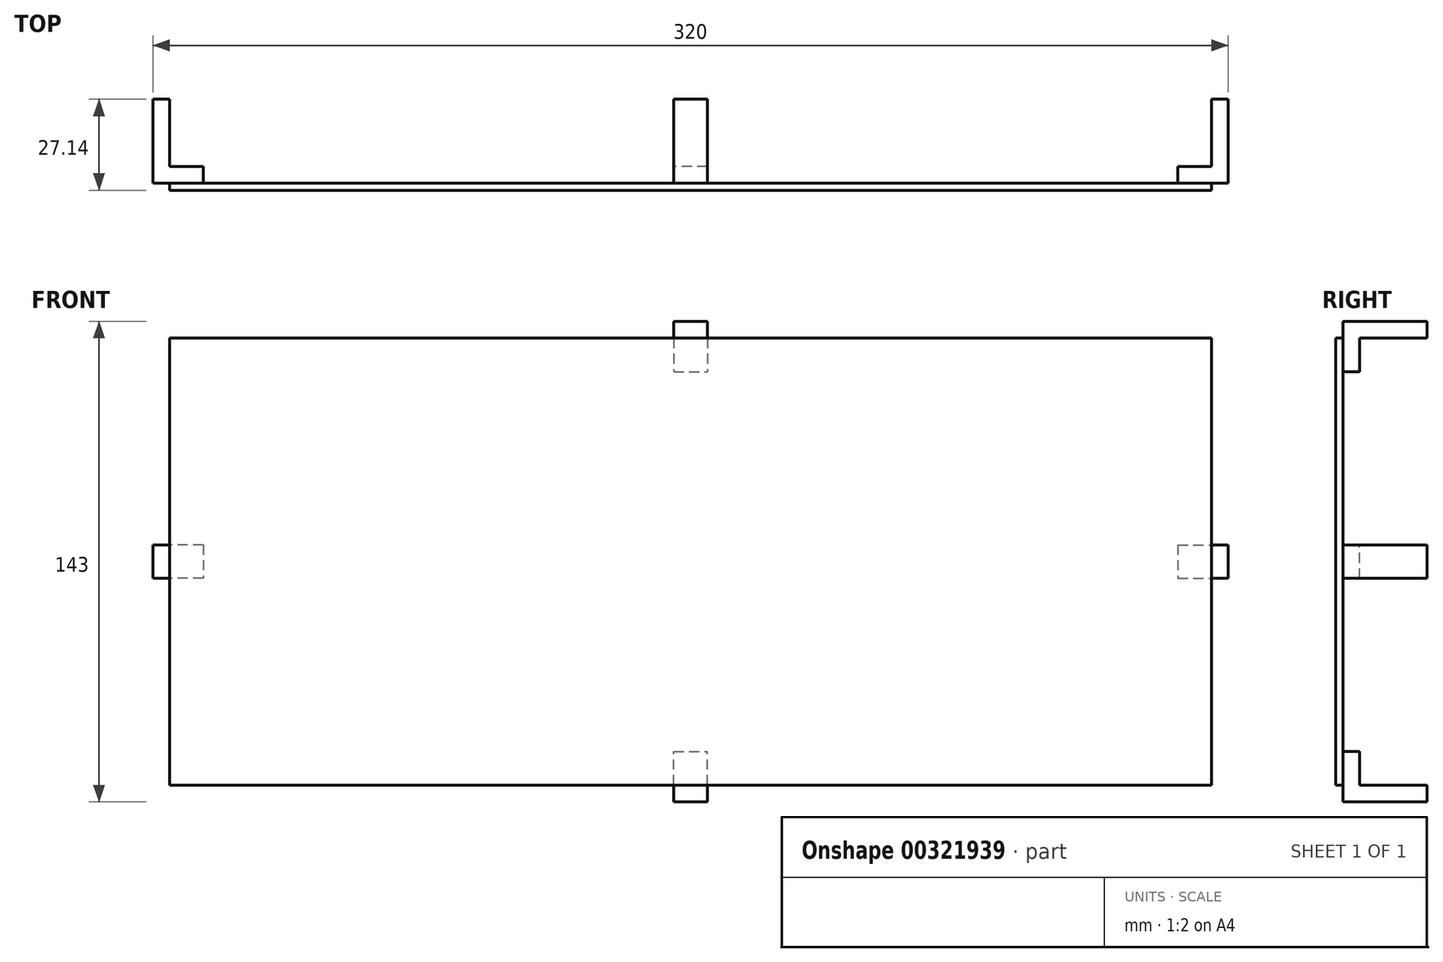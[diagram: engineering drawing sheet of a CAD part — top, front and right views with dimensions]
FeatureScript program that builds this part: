
annotation { "Feature Type Name" : "Feature", "Feature Type Description" : "" }
export const myFeature = defineFeature(function(context is Context, id is Id, definition is map)
    precondition{}
    {
        {
            var Q0;
            Q0=qCreatedBy(makeId("Front.planeOp"),FACE);
            var sketch = newSketch(context, id + "F0", { "sketchPlane" : qUnion([Q0])});
            skLineSegment(sketch, "E0.bottom", {"start": v(155, 66.5) * mm, "end": v(-155, 66.5) * mm});
            skLineSegment(sketch, "E0.top", {"start": v(155, -66.5) * mm, "end": v(-155, -66.5) * mm});
            skLineSegment(sketch, "E0.left", {"start": v(155, 66.5) * mm, "end": v(155, -66.5) * mm});
            skLineSegment(sketch, "E0.right", {"start": v(-155, 66.5) * mm, "end": v(-155, -66.5) * mm});
            skPoint(sketch, "E0.middle", {"position": v(0, 0) * mm});
            skSolve(sketch);
        }
        {
            var Q0;
            Q0 = qSketchRegion(id + "F0", true);
            extrude(context, id + "F1", {"entities" : qUnion([Q0]), "endBound" : BoundingType.SYMMETRIC, "depth" : 2.14 * mm});
        }
        {
            var Q0;
            Q0=makeQuery(id+"F1.opExtrude","CAP_FACE",FACE,{"disambiguationData":[OSD([sQuery(id+"F0.wireOp",EDGE,"E0.bottom"),sQuery(id+"F0.wireOp",EDGE,"E0.top"),sQuery(id+"F0.wireOp",EDGE,"E0.left"),sQuery(id+"F0.wireOp",EDGE,"E0.right")])],"isStart":true});
            var sketch = newSketch(context, id + "F2", { "sketchPlane" : qUnion([Q0])});
            skLineSegment(sketch, "E1.top", {"start": v(5, 56.5) * mm, "end": v(-5, 56.5) * mm});
            skLineSegment(sketch, "E1.left", {"start": v(5, 71.5) * mm, "end": v(5, 56.5) * mm});
            skLineSegment(sketch, "E1.right", {"start": v(-5, 71.5) * mm, "end": v(-5, 56.5) * mm});
            skPoint(sketch, "E1.middle", {"position": v(0, 66.5) * mm});
            skLineSegment(sketch, "E2", {"start": v(-5, 71.5) * mm, "end": v(5, 71.5) * mm});
            skPoint(sketch, "E1.bottom.end.orphan", {"position": v(-5, 76.5) * mm});
            skPoint(sketch, "E3.orphan", {"position": v(5, 76.5) * mm});
            skLineSegment(sketch, "E4.bottom", {"start": v(-145, 5) * mm, "end": v(-160, 5) * mm});
            skLineSegment(sketch, "E4.top", {"start": v(-145, -5) * mm, "end": v(-160, -5) * mm});
            skLineSegment(sketch, "E4.left", {"start": v(-145, 5) * mm, "end": v(-145, -5) * mm});
            skPoint(sketch, "E4.middle", {"position": v(-155, 0) * mm});
            skLineSegment(sketch, "E5", {"start": v(-160, 5) * mm, "end": v(-160, -5) * mm});
            skPoint(sketch, "E4.right.start.orphan", {"position": v(-165, 5) * mm});
            skPoint(sketch, "E6.orphan", {"position": v(-165, -5) * mm});
            skLineSegment(sketch, "E7.MirrorCS", {"start": v(5, -71.5) * mm, "end": v(5, -56.5) * mm});
            skLineSegment(sketch, "E8.MirrorCS", {"start": v(-5, -71.5) * mm, "end": v(-5, -56.5) * mm});
            skLineSegment(sketch, "E9.MirrorCS", {"start": v(-5, -71.5) * mm, "end": v(5, -71.5) * mm});
            skPoint(sketch, "E10.MirrorP", {"position": v(0, -66.5) * mm});
            skLineSegment(sketch, "E11.MirrorCS", {"start": v(5, -56.5) * mm, "end": v(-5, -56.5) * mm});
            skLineSegment(sketch, "E12.MirrorCS", {"start": v(145, 5) * mm, "end": v(145, -5) * mm});
            skPoint(sketch, "E13.MirrorP", {"position": v(165, -5) * mm});
            skPoint(sketch, "E14.MirrorP", {"position": v(165, 5) * mm});
            skLineSegment(sketch, "E15.MirrorCS", {"start": v(160, 5) * mm, "end": v(160, -5) * mm});
            skPoint(sketch, "E16.MirrorP", {"position": v(155, 0) * mm});
            skLineSegment(sketch, "E17.MirrorCS", {"start": v(145, -5) * mm, "end": v(160, -5) * mm});
            skLineSegment(sketch, "E18.MirrorCS", {"start": v(145, 5) * mm, "end": v(160, 5) * mm});
            skSolve(sketch);
        }
        {
            var Q0;
            Q0 = qSketchRegion(id + "F2", true);
            extrude(context, id + "F3", {"entities" : qUnion([Q0]), "operationType" : NewBodyOperationType.ADD, "depth" : 5 * mm});
        }
        {
            var Q0;
            Q0=makeQuery(id+"F3.opExtrude","CAP_FACE",FACE,{"disambiguationData":[OSD([sQuery(id+"F2.wireOp",EDGE,"E1.bottom"),sQuery(id+"F2.wireOp",EDGE,"E1.top"),sQuery(id+"F2.wireOp",EDGE,"E1.left"),sQuery(id+"F2.wireOp",EDGE,"E1.right")])],"isStart":false});
            var sketch = newSketch(context, id + "F4", { "sketchPlane" : qUnion([Q0])});
            skLineSegment(sketch, "E19.0", {"start": v(-155, 5) * mm, "end": v(-160, 5) * mm});
            skPoint(sketch, "E20.0", {"position": v(-165, 0) * mm});
            skPoint(sketch, "E21.0", {"position": v(-165, -5) * mm});
            skLineSegment(sketch, "E22.0", {"start": v(-155, -5) * mm, "end": v(-160, -5) * mm});
            skLineSegment(sketch, "E23", {"start": v(-155, -5) * mm, "end": v(-155, 5) * mm});
            skLineSegment(sketch, "E24", {"start": v(-160, -5) * mm, "end": v(-160, 5) * mm});
            skPoint(sketch, "E25.orphan", {"position": v(-165, 5) * mm});
            skPoint(sketch, "E26.MirrorP", {"position": v(165, 0) * mm});
            skLineSegment(sketch, "E27.MirrorCS", {"start": v(155, 5) * mm, "end": v(160, 5) * mm});
            skLineSegment(sketch, "E28.MirrorCS", {"start": v(155, -5) * mm, "end": v(160, -5) * mm});
            skPoint(sketch, "E29.MirrorP", {"position": v(165, -5) * mm});
            skLineSegment(sketch, "E30.MirrorCS", {"start": v(155, -5) * mm, "end": v(155, 5) * mm});
            skLineSegment(sketch, "E31.MirrorCS", {"start": v(160, -5) * mm, "end": v(160, 5) * mm});
            skPoint(sketch, "E32.MirrorP", {"position": v(165, 5) * mm});
            skLineSegment(sketch, "E33.bottom", {"start": v(-5, 71.5) * mm, "end": v(5, 71.5) * mm});
            skLineSegment(sketch, "E33.top", {"start": v(-5, 66.5) * mm, "end": v(5, 66.5) * mm});
            skLineSegment(sketch, "E33.left", {"start": v(-5, 71.5) * mm, "end": v(-5, 66.5) * mm});
            skLineSegment(sketch, "E33.right", {"start": v(5, 71.5) * mm, "end": v(5, 66.5) * mm});
            skLineSegment(sketch, "E34.MirrorCS", {"start": v(5, -71.5) * mm, "end": v(5, -66.5) * mm});
            skLineSegment(sketch, "E35.MirrorCS", {"start": v(-5, -71.5) * mm, "end": v(-5, -66.5) * mm});
            skLineSegment(sketch, "E36.MirrorCS", {"start": v(-5, -71.5) * mm, "end": v(5, -71.5) * mm});
            skLineSegment(sketch, "E37.MirrorCS", {"start": v(-5, -66.5) * mm, "end": v(5, -66.5) * mm});
            skSolve(sketch);
        }
        {
            var Q0;
            Q0 = qSketchRegion(id + "F4", true);
            extrude(context, id + "F5", {"entities" : qUnion([Q0]), "operationType" : NewBodyOperationType.ADD, "depth" : 20 * mm});
        }
    });
